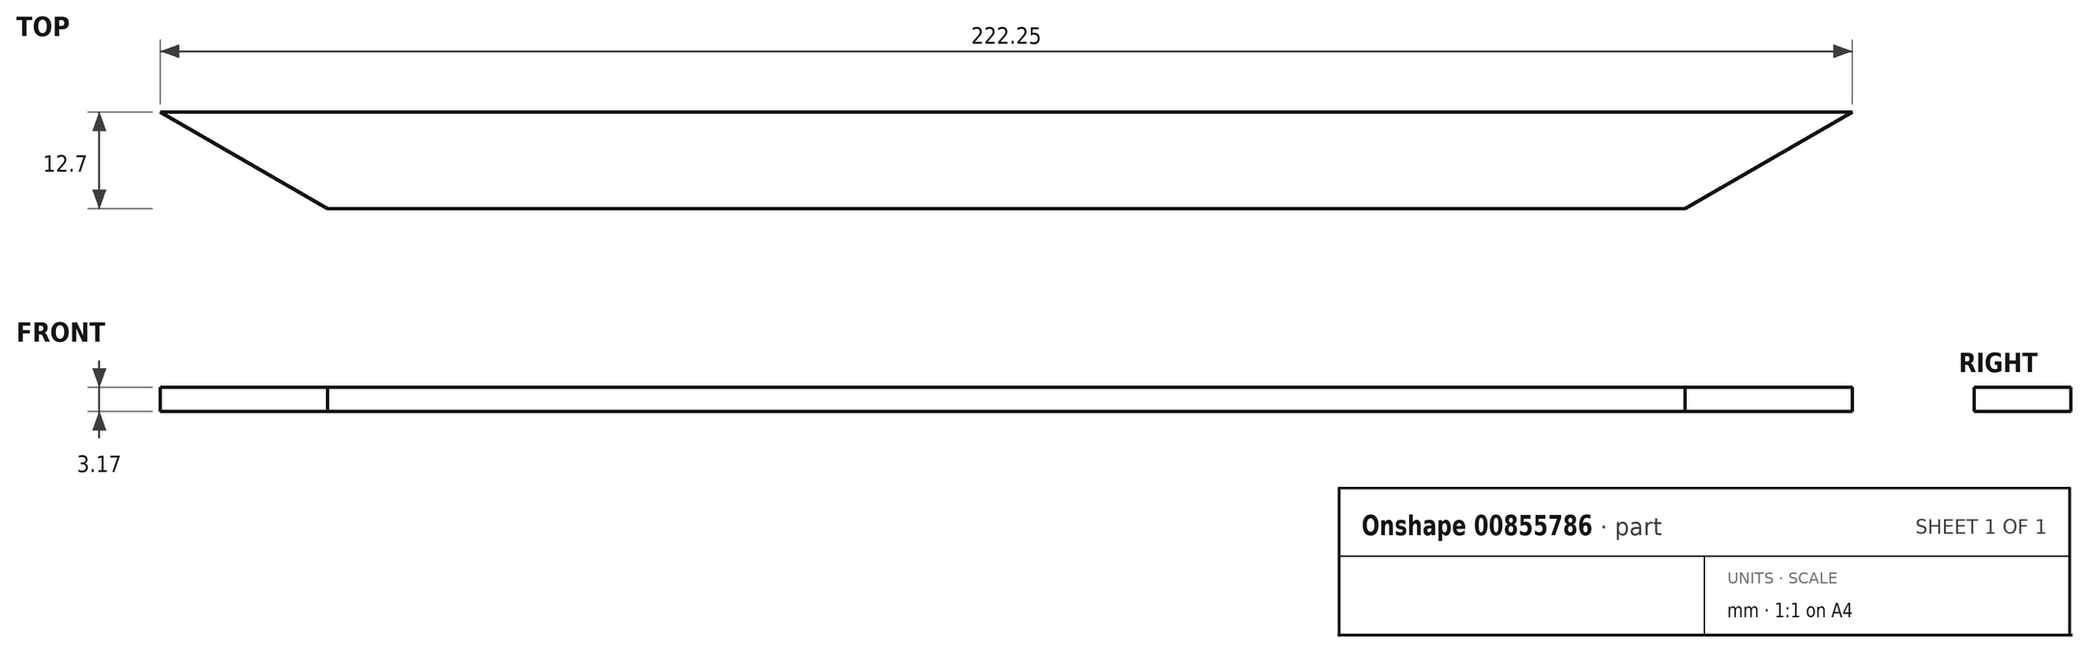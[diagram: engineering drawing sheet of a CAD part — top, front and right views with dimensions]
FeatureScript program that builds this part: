
annotation { "Feature Type Name" : "Feature", "Feature Type Description" : "" }
export const myFeature = defineFeature(function(context is Context, id is Id, definition is map)
    precondition{}
    {
        {
            var Q0;
            Q0=qCreatedBy(makeId("Top.planeOp"),FACE);
            var sketch = newSketch(context, id + "F0", { "sketchPlane" : qUnion([Q0])});
            skLineSegment(sketch, "E0", {"start": v(-108, 40.92) * mm, "end": v(114.25, 40.92) * mm});
            skLineSegment(sketch, "E1", {"start": v(114.25, 40.92) * mm, "end": v(92.25, 28.22) * mm});
            skLineSegment(sketch, "E2", {"start": v(92.25, 28.22) * mm, "end": v(-86, 28.22) * mm});
            skLineSegment(sketch, "E3", {"start": v(-86, 28.22) * mm, "end": v(-108, 40.92) * mm});
            skSolve(sketch);
        }
        {
            var Q0;
            Q0=makeQuery(id+"F0.imprint","IMPRINT",FACE,{"disambiguationData":[TD([[makeQuery(id+"F0.imprint","IMPRINT",EDGE,{"derivedFrom":sQuery(id+"F0.wireOp",EDGE,"E0")}),-1.0]])]});
            extrude(context, id + "F1", {"entities" : qUnion([Q0]), "depth" : 3.17 * mm, "offsetDistance" : 25.4 * mm});
        }
    });
